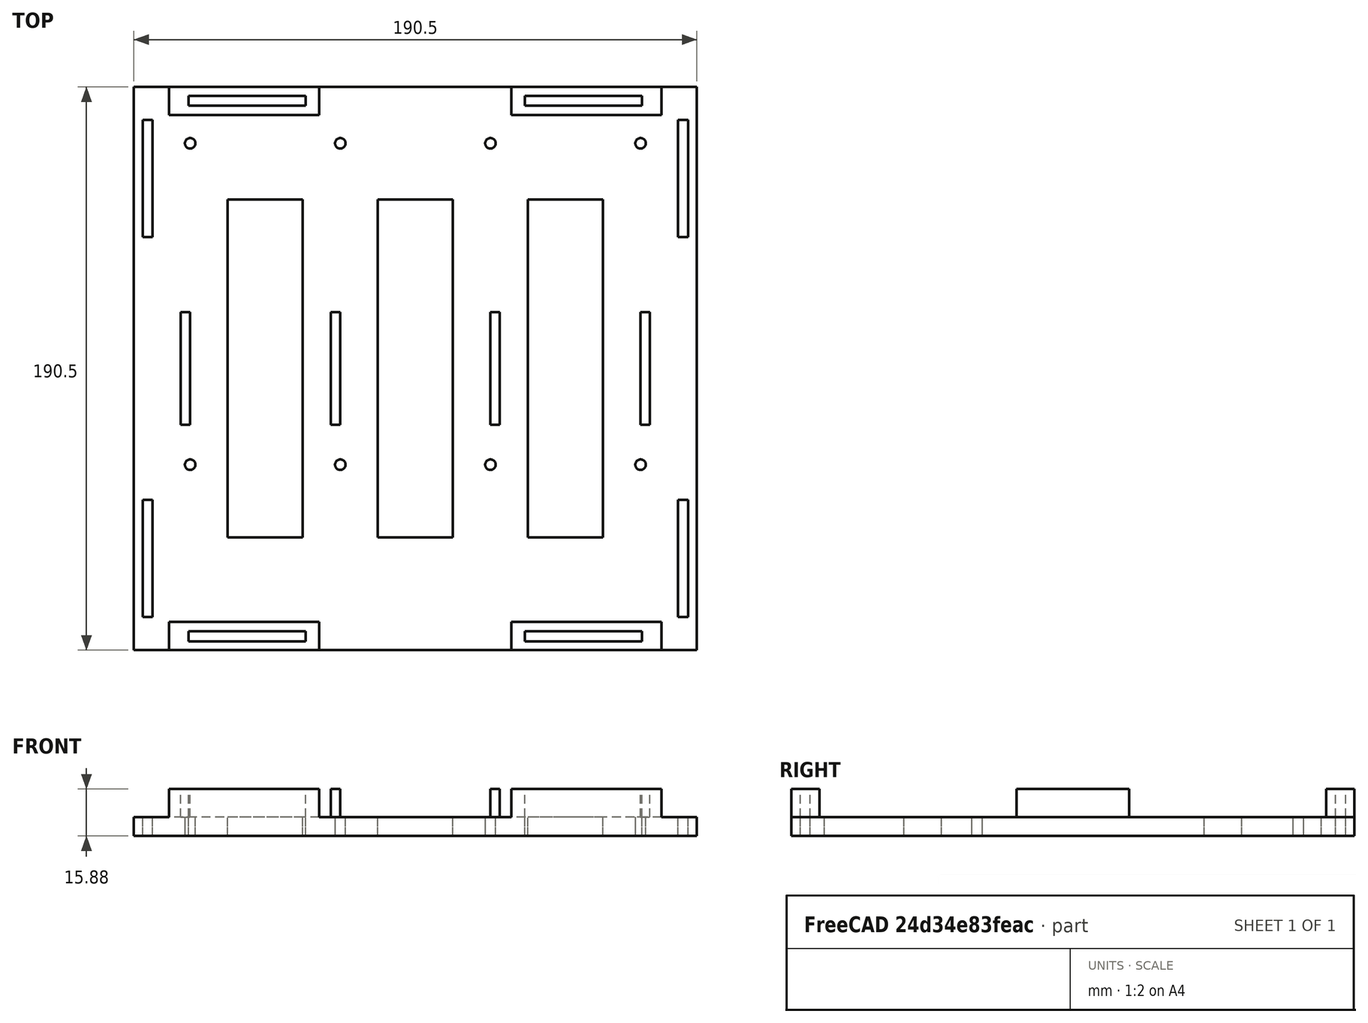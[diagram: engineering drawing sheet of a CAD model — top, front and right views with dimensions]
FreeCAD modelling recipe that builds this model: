
FCSTD DOCUMENT  (FreeCAD 0.18R4 (GitTag))
Label: bb68kv2
License: All rights reserved
LicenseURL: http://en.wikipedia.org/wiki/All_rights_reserved
objects: Sketcher::SketchObject×2, PartDesign::Pad×2, PartDesign::Body×1, App::Part×1, Mesh::Feature×1
note: 7 computed .brp shape members not serialized (recipe doc carries the construction recipe); baked Part::Feature solids carry a one-line shape summary decoded from their .brp

FEATURE [Sketcher::SketchObject] Sketch
  MapMode = 5
  Support = -> [XY_Plane001]
  sketch-geometry (56):
    g0: LineSegment StartX=-95.25 StartY=95.25 StartZ=0 EndX=95.25 EndY=95.25 EndZ=0
    g1: LineSegment StartX=95.25 StartY=95.25 StartZ=0 EndX=95.25 EndY=-95.25 EndZ=0
    g2: LineSegment StartX=95.25 StartY=-95.25 StartZ=0 EndX=-95.25 EndY=-95.25 EndZ=0
    g3: LineSegment StartX=-95.25 StartY=-95.25 StartZ=0 EndX=-95.25 EndY=95.25 EndZ=0
    g4: LineSegment StartX=-76.708 StartY=92.2528 StartZ=0 EndX=-37.084 EndY=92.2528 EndZ=0
    g5: LineSegment StartX=-37.084 StartY=92.2528 StartZ=0 EndX=-37.084 EndY=88.9 EndZ=0
    g6: LineSegment StartX=-37.084 StartY=88.9 StartZ=0 EndX=-76.708 EndY=88.9 EndZ=0
    g7: LineSegment StartX=-76.708 StartY=88.9 StartZ=0 EndX=-76.708 EndY=92.2528 EndZ=0
    g8: LineSegment StartX=37.084 StartY=-88.9 StartZ=0 EndX=76.708 EndY=-88.9 EndZ=0
    g9: LineSegment StartX=76.708 StartY=-88.9 StartZ=0 EndX=76.708 EndY=-92.2528 EndZ=0
    g10: LineSegment StartX=76.708 StartY=-92.2528 StartZ=0 EndX=37.084 EndY=-92.2528 EndZ=0
    g11: LineSegment StartX=37.084 StartY=-92.2528 StartZ=0 EndX=37.084 EndY=-88.9 EndZ=0
    g12: LineSegment StartX=-76.708 StartY=-88.9 StartZ=0 EndX=-37.084 EndY=-88.9 EndZ=0
    g13: LineSegment StartX=-37.084 StartY=-88.9 StartZ=0 EndX=-37.084 EndY=-92.2528 EndZ=0
    g14: LineSegment StartX=-37.084 StartY=-92.2528 StartZ=0 EndX=-76.708 EndY=-92.2528 EndZ=0
    g15: LineSegment StartX=-76.708 StartY=-92.2528 StartZ=0 EndX=-76.708 EndY=-88.9 EndZ=0
    g16: LineSegment StartX=37.084 StartY=92.2528 StartZ=0 EndX=76.708 EndY=92.2528 EndZ=0
    g17: LineSegment StartX=76.708 StartY=92.2528 StartZ=0 EndX=76.708 EndY=88.9 EndZ=0
    g18: LineSegment StartX=76.708 StartY=88.9 StartZ=0 EndX=37.084 EndY=88.9 EndZ=0
    g19: LineSegment StartX=37.084 StartY=88.9 StartZ=0 EndX=37.084 EndY=92.2528 EndZ=0
    g20: LineSegment StartX=-63.5 StartY=57.15 StartZ=0 EndX=-38.1 EndY=57.15 EndZ=0
    g21: LineSegment StartX=-38.1 StartY=57.15 StartZ=0 EndX=-38.1 EndY=-57.15 EndZ=0
    g22: LineSegment StartX=-38.1 StartY=-57.15 StartZ=0 EndX=-63.5 EndY=-57.15 EndZ=0
    g23: LineSegment StartX=-63.5 StartY=-57.15 StartZ=0 EndX=-63.5 EndY=57.15 EndZ=0
    g24: LineSegment StartX=-12.7 StartY=57.15 StartZ=0 EndX=12.7 EndY=57.15 EndZ=0
    g25: LineSegment StartX=12.7 StartY=57.15 StartZ=0 EndX=12.7 EndY=-57.15 EndZ=0
    g26: LineSegment StartX=12.7 StartY=-57.15 StartZ=0 EndX=-12.7 EndY=-57.15 EndZ=0
    g27: LineSegment StartX=-12.7 StartY=-57.15 StartZ=0 EndX=-12.7 EndY=57.15 EndZ=0
    g28: LineSegment StartX=38.1 StartY=57.15 StartZ=0 EndX=63.5 EndY=57.15 EndZ=0
    g29: LineSegment StartX=63.5 StartY=57.15 StartZ=0 EndX=63.5 EndY=-57.15 EndZ=0
    g30: LineSegment StartX=63.5 StartY=-57.15 StartZ=0 EndX=38.1 EndY=-57.15 EndZ=0
    g31: LineSegment StartX=38.1 StartY=-57.15 StartZ=0 EndX=38.1 EndY=57.15 EndZ=0
    g32: LineSegment StartX=-92.2528 StartY=84.074 StartZ=0 EndX=-88.9 EndY=84.074 EndZ=0
    g33: LineSegment StartX=-88.9 StartY=84.074 StartZ=0 EndX=-88.9 EndY=44.45 EndZ=0
    g34: LineSegment StartX=-88.9 StartY=44.45 StartZ=0 EndX=-92.2528 EndY=44.45 EndZ=0
    g35: LineSegment StartX=-92.2528 StartY=44.45 StartZ=0 EndX=-92.2528 EndY=84.074 EndZ=0
    g36: LineSegment StartX=88.9 StartY=84.074 StartZ=0 EndX=92.2528 EndY=84.074 EndZ=0
    g37: LineSegment StartX=92.2528 StartY=84.074 StartZ=0 EndX=92.2528 EndY=44.45 EndZ=0
    g38: LineSegment StartX=92.2528 StartY=44.45 StartZ=0 EndX=88.9 EndY=44.45 EndZ=0
    g39: LineSegment StartX=88.9 StartY=44.45 StartZ=0 EndX=88.9 EndY=84.074 EndZ=0
    g40: LineSegment StartX=-92.2528 StartY=-44.45 StartZ=0 EndX=-88.9 EndY=-44.45 EndZ=0
    g41: LineSegment StartX=-88.9 StartY=-44.45 StartZ=0 EndX=-88.9 EndY=-84.074 EndZ=0
    g42: LineSegment StartX=-88.9 StartY=-84.074 StartZ=0 EndX=-92.2528 EndY=-84.074 EndZ=0
    g43: LineSegment StartX=-92.2528 StartY=-84.074 StartZ=0 EndX=-92.2528 EndY=-44.45 EndZ=0
    g44: LineSegment StartX=88.9 StartY=-44.45 StartZ=0 EndX=92.2528 EndY=-44.45 EndZ=0
    g45: LineSegment StartX=92.2528 StartY=-44.45 StartZ=0 EndX=92.2528 EndY=-84.074 EndZ=0
    g46: LineSegment StartX=92.2528 StartY=-84.074 StartZ=0 EndX=88.9 EndY=-84.074 EndZ=0
    g47: LineSegment StartX=88.9 StartY=-84.074 StartZ=0 EndX=88.9 EndY=-44.45 EndZ=0
    g48: Circle CenterX=-76.2 CenterY=76.2 CenterZ=0 NormalX=0 NormalY=0 NormalZ=1 AngleXU=0 Radius=1.778
    g49: Circle CenterX=-25.4 CenterY=76.2 CenterZ=0 NormalX=0 NormalY=0 NormalZ=1 AngleXU=0 Radius=1.778
    g50: Circle CenterX=25.4 CenterY=76.2 CenterZ=0 NormalX=0 NormalY=0 NormalZ=1 AngleXU=0 Radius=1.778
    g51: Circle CenterX=76.2 CenterY=76.2 CenterZ=0 NormalX=0 NormalY=0 NormalZ=1 AngleXU=0 Radius=1.778
    g52: Circle CenterX=-76.2 CenterY=-32.512 CenterZ=0 NormalX=0 NormalY=0 NormalZ=1 AngleXU=0 Radius=1.778
    g53: Circle CenterX=-25.4 CenterY=-32.512 CenterZ=0 NormalX=0 NormalY=0 NormalZ=1 AngleXU=0 Radius=1.778
    g54: Circle CenterX=25.4 CenterY=-32.512 CenterZ=0 NormalX=0 NormalY=0 NormalZ=1 AngleXU=0 Radius=1.778
    g55: Circle CenterX=76.2 CenterY=-32.512 CenterZ=0 NormalX=0 NormalY=0 NormalZ=1 AngleXU=0 Radius=1.778
  constraints (153):
    c: Coincident(g0,g1)
    c: Coincident(g1,g2)
    c: Coincident(g2,g3)
    c: Coincident(g3,g0)
    c: Horizontal(g2)
    c: Vertical(g1)
    c: DistanceY(g2,g0) = 190.5
    c: DistanceX(g0,g0) = 190.5
    c: DistanceY(g-1,g0) = 95.25
    c: DistanceX(g0,g-1) = 95.25
    c: Equal(g0,g2)
    c: Equal(g3,g1)
    c: Coincident(g4,g5)
    c: Coincident(g5,g6)
    c: Coincident(g6,g7)
    c: Coincident(g7,g4)
    c: Horizontal(g4)
    c: Horizontal(g6)
    c: Vertical(g5)
    c: Vertical(g7)
    c: Coincident(g8,g9)
    c: Coincident(g9,g10)
    c: Coincident(g10,g11)
    c: Coincident(g11,g8)
    c: Horizontal(g8)
    c: Horizontal(g10)
    c: Vertical(g9)
    c: Vertical(g11)
    c: Coincident(g12,g13)
    c: Coincident(g13,g14)
    c: Coincident(g14,g15)
    c: Coincident(g15,g12)
    c: Horizontal(g12)
    c: Horizontal(g14)
    c: Vertical(g13)
    c: Vertical(g15)
    c: Coincident(g16,g17)
    c: Coincident(g17,g18)
    c: Coincident(g18,g19)
    c: Coincident(g19,g16)
    c: Horizontal(g16)
    c: Horizontal(g18)
    c: Vertical(g17)
    c: Vertical(g19)
    c: Equal(g7,g11)
    c: Equal(g11,g15)
    c: Equal(g15,g19)
    c: Equal(g4,g8)
    c: Equal(g8,g16)
    c: Equal(g16,g12)
    c: DistanceX(g4,g4) = 39.624
    c: DistanceY(g6,g4) = 3.3528
    c: Symmetric(g5,g8,g-1)
    c: Symmetric(g12,g18,g-1)
    c: Symmetric(g18,g8,g-1)
    c: Symmetric(g5,g18,g-2)
    c: DistanceX(g5,g-1) = 37.084
    c: DistanceY(g-1,g5) = 88.9
    c: Coincident(g20,g21)
    c: Coincident(g21,g22)
    c: Coincident(g22,g23)
    c: Coincident(g23,g20)
    c: Horizontal(g22)
    c: Vertical(g21)
    c: Coincident(g24,g25)
    c: Coincident(g25,g26)
    c: Coincident(g26,g27)
    c: Coincident(g27,g24)
    c: Horizontal(g26)
    c: Vertical(g25)
    c: Coincident(g28,g29)
    c: Coincident(g29,g30)
    c: Coincident(g30,g31)
    c: Coincident(g31,g28)
    c: Horizontal(g28)
    c: Horizontal(g30)
    c: Vertical(g29)
    c: Equal(g23,g27)
    c: Equal(g27,g31)
    c: Equal(g22,g26)
    c: Equal(g26,g30)
    c: DistanceX(g22,g21) = 25.4
    c: DistanceY(g22,g20) = 114.3
    c: Symmetric(g20,g22,g-1)
    c: Symmetric(g24,g26,g-1)
    c: Symmetric(g28,g30,g-1)
    c: Symmetric(g24,g24,g-2)
    c: Symmetric(g20,g28,g-2)
    c: DistanceX(g20,g-1) = 38.1
    c: Coincident(g32,g33)
    c: Coincident(g33,g34)
    c: Coincident(g34,g35)
    c: Coincident(g35,g32)
    c: Horizontal(g32)
    c: Horizontal(g34)
    c: Vertical(g33)
    c: Vertical(g35)
    c: Coincident(g36,g37)
    c: Coincident(g37,g38)
    c: Coincident(g38,g39)
    c: Coincident(g39,g36)
    c: Horizontal(g36)
    c: Horizontal(g38)
    c: Vertical(g37)
    c: Vertical(g39)
    c: Coincident(g40,g41)
    c: Coincident(g41,g42)
    c: Coincident(g42,g43)
    c: Coincident(g43,g40)
    c: Horizontal(g40)
    c: Horizontal(g42)
    c: Vertical(g41)
    c: Vertical(g43)
    c: Coincident(g44,g45)
    c: Coincident(g45,g46)
    c: Coincident(g46,g47)
    c: Coincident(g47,g44)
    c: Horizontal(g44)
    c: Horizontal(g46)
    c: Vertical(g45)
    c: Vertical(g47)
    c: Equal(g32,g36)
    c: Equal(g36,g40)
    c: Equal(g40,g44)
    c: DistanceX(g32,g32) = 3.3528
    c: Equal(g35,g39)
    c: Equal(g39,g43)
    c: Equal(g43,g47)
    c: DistanceY(g34,g32) = 39.624
    c: Symmetric(g33,g44,g-1)
    c: Symmetric(g40,g38,g-1)
    c: Symmetric(g33,g40,g-1)
    c: Symmetric(g33,g38,g-2)
    c: DistanceX(g33,g-1) = 88.9
    c: DistanceY(g-1,g33) = 44.45
    c: Diameter(g48) = 3.556
    c: Equal(g48, g49-g55) x7
    c: DistanceX(g48,g-1) = 76.2
    c: DistanceX(g49,g-1) = 25.4
    c: DistanceX(g-1,g50) = 25.4
    c: DistanceX(g-1,g51) = 76.2
    c: DistanceY(g-1,g48) = 76.2
    c: DistanceY(g48,g49) = 0
    c: DistanceY(g49,g50) = 0
    c: DistanceY(g50,g51) = 0
    c: DistanceX(g48,g52) = 0
    c: DistanceX(g49,g53) = 0
    c: DistanceX(g50,g54) = 0
    c: DistanceX(g51,g55) = 0
    c: DistanceY(g52,g48) = 108.712
    c: DistanceY(g53,g49) = 108.712
    c: DistanceY(g54,g50) = 108.712
    c: DistanceY(g55,g51) = 108.712
FEATURE [Sketcher::SketchObject] Sketch001
  MapMode = 5
  Placement = pos=(0,0,3.175) rot=(0,0,1;0rad)
  sketch-geometry (48):
    g0: LineSegment StartX=-83.312 StartY=95.25 StartZ=0 EndX=-32.512 EndY=95.25 EndZ=0
    g1: LineSegment StartX=-32.512 StartY=95.25 StartZ=0 EndX=-32.512 EndY=85.725 EndZ=0
    g2: LineSegment StartX=-32.512 StartY=85.725 StartZ=0 EndX=-83.312 EndY=85.725 EndZ=0
    g3: LineSegment StartX=-83.312 StartY=85.725 StartZ=0 EndX=-83.312 EndY=95.25 EndZ=0
    g4: LineSegment StartX=32.512 StartY=95.25 StartZ=0 EndX=83.312 EndY=95.25 EndZ=0
    g5: LineSegment StartX=83.312 StartY=95.25 StartZ=0 EndX=83.312 EndY=85.725 EndZ=0
    g6: LineSegment StartX=83.312 StartY=85.725 StartZ=0 EndX=32.512 EndY=85.725 EndZ=0
    g7: LineSegment StartX=32.512 StartY=85.725 StartZ=0 EndX=32.512 EndY=95.25 EndZ=0
    g8: LineSegment StartX=-83.312 StartY=-85.725 StartZ=0 EndX=-32.512 EndY=-85.725 EndZ=0
    g9: LineSegment StartX=-32.512 StartY=-85.725 StartZ=0 EndX=-32.512 EndY=-95.25 EndZ=0
    g10: LineSegment StartX=-32.512 StartY=-95.25 StartZ=0 EndX=-83.312 EndY=-95.25 EndZ=0
    g11: LineSegment StartX=-83.312 StartY=-95.25 StartZ=0 EndX=-83.312 EndY=-85.725 EndZ=0
    g12: LineSegment StartX=32.512 StartY=-85.725 StartZ=0 EndX=83.312 EndY=-85.725 EndZ=0
    g13: LineSegment StartX=83.312 StartY=-85.725 StartZ=0 EndX=83.312 EndY=-95.25 EndZ=0
    g14: LineSegment StartX=83.312 StartY=-95.25 StartZ=0 EndX=32.512 EndY=-95.25 EndZ=0
    g15: LineSegment StartX=32.512 StartY=-95.25 StartZ=0 EndX=32.512 EndY=-85.725 EndZ=0
    g16: LineSegment StartX=-76.708 StartY=92.2528 StartZ=0 EndX=-37.084 EndY=92.2528 EndZ=0
    g17: LineSegment StartX=-37.084 StartY=92.2528 StartZ=0 EndX=-37.084 EndY=88.9 EndZ=0
    g18: LineSegment StartX=-37.084 StartY=88.9 StartZ=0 EndX=-76.708 EndY=88.9 EndZ=0
    g19: LineSegment StartX=-76.708 StartY=88.9 StartZ=0 EndX=-76.708 EndY=92.2528 EndZ=0
    g20: LineSegment StartX=37.084 StartY=92.2528 StartZ=0 EndX=76.708 EndY=92.2528 EndZ=0
    g21: LineSegment StartX=76.708 StartY=92.2528 StartZ=0 EndX=76.708 EndY=88.9 EndZ=0
    g22: LineSegment StartX=76.708 StartY=88.9 StartZ=0 EndX=37.084 EndY=88.9 EndZ=0
    g23: LineSegment StartX=37.084 StartY=88.9 StartZ=0 EndX=37.084 EndY=92.2528 EndZ=0
    g24: LineSegment StartX=-76.708 StartY=-88.9 StartZ=0 EndX=-37.084 EndY=-88.9 EndZ=0
    g25: LineSegment StartX=-37.084 StartY=-88.9 StartZ=0 EndX=-37.084 EndY=-92.2528 EndZ=0
    g26: LineSegment StartX=-37.084 StartY=-92.2528 StartZ=0 EndX=-76.708 EndY=-92.2528 EndZ=0
    g27: LineSegment StartX=-76.708 StartY=-92.2528 StartZ=0 EndX=-76.708 EndY=-88.9 EndZ=0
    g28: LineSegment StartX=37.084 StartY=-88.9 StartZ=0 EndX=76.708 EndY=-88.9 EndZ=0
    g29: LineSegment StartX=76.708 StartY=-88.9 StartZ=0 EndX=76.708 EndY=-92.2528 EndZ=0
    g30: LineSegment StartX=76.708 StartY=-92.2528 StartZ=0 EndX=37.084 EndY=-92.2528 EndZ=0
    g31: LineSegment StartX=37.084 StartY=-92.2528 StartZ=0 EndX=37.084 EndY=-88.9 EndZ=0
    g32: LineSegment StartX=-79.375 StartY=19.05 StartZ=0 EndX=-76.2 EndY=19.05 EndZ=0
    g33: LineSegment StartX=-76.2 StartY=19.05 StartZ=0 EndX=-76.2 EndY=-19.05 EndZ=0
    g34: LineSegment StartX=-76.2 StartY=-19.05 StartZ=0 EndX=-79.375 EndY=-19.05 EndZ=0
    g35: LineSegment StartX=-79.375 StartY=-19.05 StartZ=0 EndX=-79.375 EndY=19.05 EndZ=0
    g36: LineSegment StartX=-28.575 StartY=19.05 StartZ=0 EndX=-25.4 EndY=19.05 EndZ=0
    g37: LineSegment StartX=-25.4 StartY=19.05 StartZ=0 EndX=-25.4 EndY=-19.05 EndZ=0
    g38: LineSegment StartX=-25.4 StartY=-19.05 StartZ=0 EndX=-28.575 EndY=-19.05 EndZ=0
    g39: LineSegment StartX=-28.575 StartY=-19.05 StartZ=0 EndX=-28.575 EndY=19.05 EndZ=0
    g40: LineSegment StartX=25.4 StartY=19.05 StartZ=0 EndX=28.575 EndY=19.05 EndZ=0
    g41: LineSegment StartX=28.575 StartY=19.05 StartZ=0 EndX=28.575 EndY=-19.05 EndZ=0
    g42: LineSegment StartX=28.575 StartY=-19.05 StartZ=0 EndX=25.4 EndY=-19.05 EndZ=0
    g43: LineSegment StartX=25.4 StartY=-19.05 StartZ=0 EndX=25.4 EndY=19.05 EndZ=0
    g44: LineSegment StartX=76.2 StartY=19.05 StartZ=0 EndX=79.375 EndY=19.05 EndZ=0
    g45: LineSegment StartX=79.375 StartY=19.05 StartZ=0 EndX=79.375 EndY=-19.05 EndZ=0
    g46: LineSegment StartX=79.375 StartY=-19.05 StartZ=0 EndX=76.2 EndY=-19.05 EndZ=0
    g47: LineSegment StartX=76.2 StartY=-19.05 StartZ=0 EndX=76.2 EndY=19.05 EndZ=0
  constraints (138):
    c: Coincident(g0,g1)
    c: Coincident(g1,g2)
    c: Coincident(g2,g3)
    c: Coincident(g3,g0)
    c: Horizontal(g0)
    c: Horizontal(g2)
    c: Vertical(g1)
    c: Vertical(g3)
    c: Coincident(g4,g5)
    c: Coincident(g5,g6)
    c: Coincident(g6,g7)
    c: Coincident(g7,g4)
    c: Horizontal(g4)
    c: Horizontal(g6)
    c: Vertical(g5)
    c: Vertical(g7)
    c: Coincident(g8,g9)
    c: Coincident(g9,g10)
    c: Coincident(g10,g11)
    c: Coincident(g11,g8)
    c: Horizontal(g8)
    c: Horizontal(g10)
    c: Vertical(g9)
    c: Vertical(g11)
    c: Coincident(g12,g13)
    c: Coincident(g13,g14)
    c: Coincident(g14,g15)
    c: Coincident(g15,g12)
    c: Horizontal(g12)
    c: Horizontal(g14)
    c: Vertical(g13)
    c: Vertical(g15)
    c: Equal(g3,g7)
    c: Equal(g7,g11)
    c: Equal(g11,g15)
    c: Equal(g2,g6)
    c: Equal(g6,g8)
    c: Equal(g8,g12)
    c: Symmetric(g1,g12,g-1)
    c: Symmetric(g8,g6,g-1)
    c: Symmetric(g1,g8,g-1)
    c: Symmetric(g1,g6,g-2)
    c: DistanceY(g-1,g1) = 85.725
    c: DistanceX(g1,g-1) = 32.512
    c: DistanceY(g2,g0) = 9.525
    c: DistanceX(g0,g0) = 50.8
    c: Coincident(g16,g17)
    c: Coincident(g17,g18)
    c: Coincident(g18,g19)
    c: Coincident(g19,g16)
    c: Horizontal(g16)
    c: Horizontal(g18)
    c: Vertical(g17)
    c: Vertical(g19)
    c: Coincident(g20,g21)
    c: Coincident(g21,g22)
    c: Coincident(g22,g23)
    c: Coincident(g23,g20)
    c: Horizontal(g20)
    c: Horizontal(g22)
    c: Vertical(g21)
    c: Vertical(g23)
    c: Coincident(g24,g25)
    c: Coincident(g25,g26)
    c: Coincident(g26,g27)
    c: Coincident(g27,g24)
    c: Horizontal(g24)
    c: Horizontal(g26)
    c: Vertical(g25)
    c: Vertical(g27)
    c: Coincident(g28,g29)
    c: Coincident(g29,g30)
    c: Coincident(g30,g31)
    c: Coincident(g31,g28)
    c: Horizontal(g28)
    c: Horizontal(g30)
    c: Vertical(g29)
    c: Vertical(g31)
    c: Equal(g19,g23)
    c: Equal(g23,g27)
    c: Equal(g27,g31)
    c: Equal(g16,g20)
    c: Equal(g20,g24)
    c: Equal(g24,g28)
    c: DistanceY(g18,g16) = 3.3528
    c: DistanceX(g16,g16) = 39.624
    c: Symmetric(g17,g28,g-1)
    c: Symmetric(g24,g22,g-1)
    c: Symmetric(g17,g24,g-1)
    c: Symmetric(g22,g28,g-1)
    c: Symmetric(g17,g22,g-2)
    c: Symmetric(g24,g28,g-2)
    c: DistanceX(g17,g-1) = 37.084
    c: DistanceY(g-1,g17) = 88.9
    c: Coincident(g32,g33)
    c: Coincident(g33,g34)
    c: Coincident(g34,g35)
    c: Coincident(g35,g32)
    c: Horizontal(g32)
    c: Horizontal(g34)
    c: Vertical(g33)
    c: Coincident(g36,g37)
    c: Coincident(g37,g38)
    c: Coincident(g38,g39)
    c: Coincident(g39,g36)
    c: Horizontal(g36)
    c: Horizontal(g38)
    c: Vertical(g37)
    c: Coincident(g40,g41)
    c: Coincident(g41,g42)
    c: Coincident(g42,g43)
    c: Coincident(g43,g40)
    c: Horizontal(g40)
    c: Horizontal(g42)
    c: Vertical(g41)
    c: Vertical(g43)
    c: Coincident(g44,g45)
    c: Coincident(g45,g46)
    c: Coincident(g46,g47)
    c: Coincident(g47,g44)
    c: Horizontal(g44)
    c: Horizontal(g46)
    c: Vertical(g45)
    c: Vertical(g47)
    c: Equal(g35,g39)
    c: Equal(g39,g43)
    c: Equal(g43,g47)
    c: Equal(g32,g36)
    c: Equal(g36,g40)
    c: Equal(g40,g44)
    c: Symmetric(g32,g46,g-1)
    c: Symmetric(g36,g42,g-1)
    c: Symmetric(g32,g34,g-1)
    c: DistanceY(g34,g32) = 38.1
    c: DistanceX(g32,g32) = 3.175
    c: Symmetric(g36,g38,g-1)
    c: DistanceX(g32,g36) = 50.8
    c: DistanceX(g36,g-1) = 28.575
FEATURE [PartDesign::Pad] Pad001
  Length = 9.525
  Length2 = 99.9998
  Placement = pos=(0,0,3.175) rot=(0,0,1;0rad)
  Profile = -> Sketch001
  Type = 0
FEATURE [PartDesign::Pad] Pad
  BaseFeature = -> Pad001
  Length = 3.175
  Length2 = 99.9998
  Placement = pos=(0,0,3.175) rot=(0,0,1;0rad)
  Profile = -> Sketch
  Type = 0
FEATURE [PartDesign::Body] Body
  Group = -> [Sketch,Sketch001,Pad001,Pad]
  Origin = -> Origin001
  Tip = -> Pad
FEATURE [App::Part] Part
  Group = -> [Body]
  Origin = -> Origin
FEATURE [Mesh::Feature] Mesh  label="bb68kv2"
